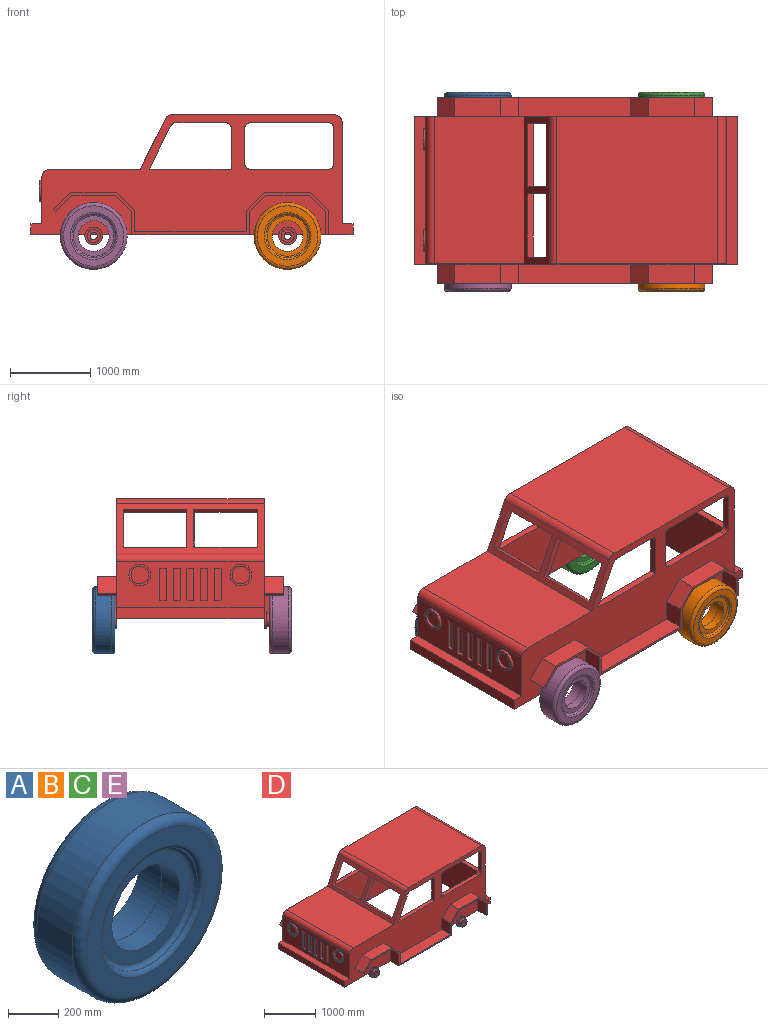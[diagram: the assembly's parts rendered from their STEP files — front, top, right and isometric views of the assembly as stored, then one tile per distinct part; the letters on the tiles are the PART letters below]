
ASSEMBLY  parts=5 mates=6
PART A: 11 faces, bbox 900.6x280x900.6 mm
  f0: torus R=292mm, axis (0,-1,0), area 55125.2mm2, adj f1,f10
  f1: plane 752x752mm, normal (0,-1,0), area 176281mm2, adj f0,f2
  f2: torus R=376mm, axis (0,-1,0), area 158491.9mm2, adj f1,f3
  f3: cylinder r=416mm len=832mm, axis (0,-1,0), area 522761mm2, adj f2,f4
  f4: torus R=376mm, axis (0,-1,0), area 158491.9mm2, adj f3,f5
  f5: plane 752x752mm, normal (0,1,0), area 308227.9mm2, adj f4,f6
  f6: cylinder r=208mm len=416mm, axis (0,-1,0), area 182966.4mm2, adj f5,f7
  f7: plane 416x416mm, normal (0,1,0), area 20106.2mm2, adj f6,f8
  f8: cylinder r=192mm len=384mm, axis (0,-1,0), area 120637.2mm2, adj f7,f9
  f9: plane 504x504mm, normal (0,-1,0), area 83692mm2, adj f8,f10
  f10: torus R=252mm, axis (0,-1,0), area 52256.1mm2, adj f0,f9
PART B: same geometry as A
PART C: same geometry as A
PART D: 174 faces, bbox 4012x2312x1623.2 mm
  f0: plane 1836x578mm, normal (-1,0,0), area 771594.2mm2, adj f3,f4,f19,f20,f74,f78,f149,f150
  f1: plane 81.89x27.55mm, normal (0,1,0), area 1632.8mm2, adj f11,f148
  f2: plane 81.89x27.55mm, normal (0,1,0), area 1632.8mm2, adj f11,f142
  f3: plane 4012x1496mm, normal (0,1,0), area 2936341.1mm2, adj f0,f11,f12,f13,f14,f15,f16,f17
  f4: plane 4012x1496mm, normal (0,-1,0), area 2936341.1mm2, adj f0,f11,f12,f13,f14,f15,f16,f17
  f5: plane 1666x1343mm, normal (-1,0,0), area 1386622mm2, adj f8,f9,f23,f24,f67,f68,f69,f70
  f6: plane 952.71x493.35mm, normal (0,-1,0), area 412746.6mm2, adj f11,f81,f82,f98,f99,f100,f132
  f7: plane 952.71x493.35mm, normal (0,1,0), area 412746.6mm2, adj f11,f102,f103,f119,f120,f121,f144
  f8: plane 3842x1411mm, normal (0,1,0), area 3073874.4mm2, adj f5,f10,f11,f13,f17,f23,f24,f25
  f9: plane 3842x1411mm, normal (0,-1,0), area 3073874.4mm2, adj f5,f10,f11,f13,f17,f23,f24,f25
  f10: plane 1666.02x670.62mm, normal (0.89,0,-0.45), area 415553.8mm2, adj f8,f9,f26,f27,f33,f34,f35,f36
  f11: plane 4012x2312mm, normal (0,0,-1), area 1666218.8mm2, adj f1,f2,f3,f4,f6,f7,f8,f9
  f12: plane 1836x136mm, normal (0,0,1), area 249696mm2, adj f3,f4,f13,f22
  f13: plane 1836x1258mm, normal (1,0,0), area 1458872mm2, adj f3,f4,f8,f9,f12,f14,f67,f68
  f14: cylinder r=102mm len=1836mm, axis (0,1,0), area 294166.2mm2, adj f3,f4,f13,f15
  f15: plane 2010.96x1836mm, normal (0,0,1), area 3692123.5mm2, adj f3,f4,f14,f16
  f16: cylinder r=102mm len=1836mm, axis (0,1,0), area 207338mm2, adj f3,f4,f15,f17
  f17: plane 1836.02x623.63mm, normal (-0.89,0,0.45), area 446562mm2, adj f3,f4,f8,f9,f16,f18,f33,f34
  f18: plane 1836x1122mm, normal (0,0,1), area 2059992mm2, adj f3,f4,f17,f19
  f19: cylinder r=102mm len=1836mm, axis (0,1,0), area 294166.2mm2, adj f0,f3,f4,f18
  f20: plane 1836x136mm, normal (0,0,1), area 249696mm2, adj f0,f3,f4,f21
  f21: plane 1836x136mm, normal (-1,0,0), area 249696mm2, adj f3,f4,f11,f20
  f22: plane 1836x136mm, normal (1,0,0), area 249696mm2, adj f3,f4,f11,f12
  f23: plane 1666x136mm, normal (0,0,-1), area 226576mm2, adj f5,f8,f9,f32
  f24: cylinder r=17mm len=1666mm, axis (0,1,0), area 44488.1mm2, adj f5,f8,f9,f25
  f25: plane 2010.96x1666mm, normal (0,0,-1), area 3350260.2mm2, adj f8,f9,f24,f26
  f26: cylinder r=17mm len=1666mm, axis (0,1,0), area 31356.7mm2, adj f8,f9,f10,f25
  f27: plane 1666x1174.53mm, normal (0,0,-1), area 1956771.8mm2, adj f8,f9,f10,f28
  f28: cylinder r=17mm len=1666mm, axis (0,1,0), area 44488.1mm2, adj f8,f9,f27,f29
  f29: plane 1666x663mm, normal (1,0,0), area 1104558mm2, adj f8,f9,f28,f30
  f30: plane 1666x136mm, normal (0,0,-1), area 226576mm2, adj f8,f9,f29,f31
  f31: plane 1666x51mm, normal (1,0,0), area 84966mm2, adj f8,f9,f11,f30
  f32: plane 1666x51mm, normal (-1,0,0), area 84966mm2, adj f8,f9,f11,f23
  f33: plane 790.52x76.05mm, normal (0.45,0,0.89), area 67192.5mm2, adj f8,f10,f17,f34
  f34: plane 509.58x311.81mm, normal (0,-1,0), area 44814mm2, adj f10,f17,f33,f35
  f35: plane 790.52x76.05mm, normal (-0.45,0,-0.89), area 67192.5mm2, adj f8,f10,f17,f34
  f36: plane 790.52x76.05mm, normal (-0.45,0,-0.89), area 67192.5mm2, adj f9,f10,f17,f37
  f37: plane 509.58x311.81mm, normal (0,1,0), area 44814mm2, adj f10,f17,f36,f38
  f38: plane 790.52x76.05mm, normal (0.45,0,0.89), area 67192.5mm2, adj f9,f10,f17,f37
  f39: plane 442x85mm, normal (1,0,0), area 37570mm2, adj f3,f9,f40,f46
  f40: cylinder r=68mm len=85mm, axis (0,-1,0), area 9079.2mm2, adj f3,f9,f39,f41
  f41: plane 973.96x85mm, normal (0,0,-1), area 82786.6mm2, adj f3,f9,f40,f42
  f42: cylinder r=68mm len=85mm, axis (0,-1,0), area 9079.2mm2, adj f3,f9,f41,f43
  f43: plane 442x85mm, normal (-1,0,0), area 37570mm2, adj f3,f9,f42,f44
  f44: cylinder r=68mm len=85mm, axis (0,-1,0), area 9079.2mm2, adj f3,f9,f43,f45
  f45: plane 973.96x85mm, normal (0,0,1), area 82786.6mm2, adj f3,f9,f44,f46
  f46: cylinder r=68mm len=85mm, axis (0,-1,0), area 9079.2mm2, adj f3,f9,f39,f45
  f47: plane 1020x85mm, normal (0,0,1), area 86700mm2, adj f3,f9,f48,f52
  f48: plane 540.41x270.21mm, normal (0.89,0,-0.45), area 51356.8mm2, adj f3,f9,f47,f49
  f49: cylinder r=68mm len=85mm, axis (0,-1,0), area 6399.3mm2, adj f3,f9,f48,f50
  f50: plane 620.97x85mm, normal (0,0,-1), area 52782.8mm2, adj f3,f9,f49,f51
  f51: cylinder r=68mm len=85mm, axis (0,-1,0), area 9079.2mm2, adj f3,f9,f50,f52
  f52: plane 510x85mm, normal (-1,0,0), area 43350mm2, adj f3,f9,f47,f51
  f53: cylinder r=68mm len=85mm, axis (0,-1,0), area 9079.2mm2, adj f4,f8,f54,f60
  f54: plane 973.96x85mm, normal (0,0,1), area 82786.6mm2, adj f4,f8,f53,f55
  f55: cylinder r=68mm len=85mm, axis (0,-1,0), area 9079.2mm2, adj f4,f8,f54,f56
  f56: plane 442x85mm, normal (-1,0,0), area 37570mm2, adj f4,f8,f55,f57
  f57: cylinder r=68mm len=85mm, axis (0,-1,0), area 9079.2mm2, adj f4,f8,f56,f58
  f58: plane 973.96x85mm, normal (0,0,-1), area 82786.6mm2, adj f4,f8,f57,f59
  f59: cylinder r=68mm len=85mm, axis (0,-1,0), area 9079.2mm2, adj f4,f8,f58,f60
  f60: plane 442x85mm, normal (1,0,0), area 37570mm2, adj f4,f8,f53,f59
  f61: plane 510x85mm, normal (-1,0,0), area 43350mm2, adj f4,f8,f62,f66
  f62: cylinder r=68mm len=85mm, axis (0,-1,0), area 9079.2mm2, adj f4,f8,f61,f63
  f63: plane 620.97x85mm, normal (0,0,-1), area 52782.8mm2, adj f4,f8,f62,f64
  f64: cylinder r=68mm len=85mm, axis (0,-1,0), area 6399.3mm2, adj f4,f8,f63,f65
  f65: plane 540.41x270.21mm, normal (0.89,0,-0.45), area 51356.8mm2, adj f4,f8,f64,f66
  f66: plane 1020x85mm, normal (0,0,1), area 86700mm2, adj f4,f8,f61,f65
  f67: plane 782x85mm, normal (0,0,-1), area 66470mm2, adj f5,f8,f13,f68
  f68: plane 544x85mm, normal (0,-1,0), area 46240mm2, adj f5,f13,f67,f69
  f69: plane 782x85mm, normal (0,0,1), area 66470mm2, adj f5,f8,f13,f68
  f70: plane 782x85mm, normal (0,0,-1), area 66470mm2, adj f5,f9,f13,f71
  f71: plane 544x85mm, normal (0,1,0), area 46240mm2, adj f5,f13,f70,f72
  f72: plane 782x85mm, normal (0,0,1), area 66470mm2, adj f5,f9,f13,f71
  f73: cylinder r=110.5mm len=221mm, axis (1,0,0), area 23605.9mm2, adj f75,f76
  f74: cylinder r=136mm len=272mm, axis (1,0,0), area 29053.4mm2, adj f0,f75
  f75: plane 272x272mm, normal (-1,0,0), area 19747.3mm2, adj f73,f74
  f76: plane 221x221mm, normal (-1,0,0), area 38359.6mm2, adj f73
  f77: cylinder r=110.5mm len=221mm, axis (1,0,0), area 23605.9mm2, adj f79,f80
  f78: cylinder r=136mm len=272mm, axis (1,0,0), area 29053.4mm2, adj f0,f79
  f79: plane 272x272mm, normal (-1,0,0), area 19747.3mm2, adj f77,f78
  f80: plane 221x221mm, normal (-1,0,0), area 38359.6mm2, adj f77
  f81: plane 238x204.35mm, normal (-0.71,0,-0.71), area 68782mm2, adj f6,f82,f100,f101
  f82: plane 289x238mm, normal (-1,0,0), area 68782mm2, adj f6,f11,f81,f101
  f83: plane 303.08x238mm, normal (1,0,0), area 72133.8mm2, adj f4,f11,f84,f101
  f84: plane 238x224.27mm, normal (0.71,0,0.71), area 75485.6mm2, adj f4,f83,f85,f101
  f85: plane 572.17x238mm, normal (0,0,1), area 136175.6mm2, adj f4,f84,f86,f101
  f86: plane 238x224.27mm, normal (-0.71,0,0.71), area 75485.6mm2, adj f4,f85,f87,f101
  f87: plane 269.08x238mm, normal (-1,0,0), area 64041.8mm2, adj f4,f86,f88,f101
  f88: plane 1394x238mm, normal (0,0,1), area 331772mm2, adj f4,f87,f89,f101
  f89: plane 269.08x238mm, normal (1,0,0), area 64041.8mm2, adj f4,f88,f90,f101
  f90: plane 238x224.27mm, normal (0.71,0,0.71), area 75485.6mm2, adj f4,f89,f91,f101
  f91: plane 572.17x238mm, normal (0,0,1), area 136175.6mm2, adj f4,f90,f92,f101
  f92: plane 238x214.31mm, normal (-0.71,0,0.71), area 72133.8mm2, adj f4,f91,f93,f101
  f93: plane 238x24.04mm, normal (-0.71,0,-0.71), area 8092mm2, adj f4,f92,f94,f101
  f94: plane 238x204.35mm, normal (0.71,0,-0.71), area 68782mm2, adj f4,f93,f95,f101
  f95: plane 544x238mm, normal (0,0,-1), area 129472mm2, adj f4,f94,f96,f101
  f96: plane 238x204.35mm, normal (-0.71,0,-0.71), area 68782mm2, adj f4,f95,f97,f101
  f97: plane 289x238mm, normal (-1,0,0), area 68782mm2, adj f4,f11,f96,f101
  f98: plane 289x238mm, normal (1,0,0), area 68782mm2, adj f6,f11,f99,f101
  f99: plane 238x204.35mm, normal (0.71,0,-0.71), area 68782mm2, adj f6,f98,f100,f101
  f100: plane 544x238mm, normal (0,0,-1), area 129472mm2, adj f6,f81,f99,f101
  f101: plane 3425.46x527.35mm, normal (0,-1,0), area 156521.8mm2, adj f11,f81,f82,f83,f84,f85,f86,f87
  f102: plane 238x204.35mm, normal (-0.71,0,-0.71), area 68782mm2, adj f7,f103,f121,f122
  f103: plane 289x238mm, normal (-1,0,0), area 68782mm2, adj f7,f11,f102,f122
  f104: plane 303.08x238mm, normal (1,0,0), area 72133.8mm2, adj f3,f11,f105,f122
  f105: plane 238x224.27mm, normal (0.71,0,0.71), area 75485.6mm2, adj f3,f104,f106,f122
  f106: plane 572.17x238mm, normal (0,0,1), area 136175.6mm2, adj f3,f105,f107,f122
  f107: plane 238x224.27mm, normal (-0.71,0,0.71), area 75485.6mm2, adj f3,f106,f108,f122
  f108: plane 269.08x238mm, normal (-1,0,0), area 64041.8mm2, adj f3,f107,f109,f122
  f109: plane 1394x238mm, normal (0,0,1), area 331772mm2, adj f3,f108,f110,f122
  f110: plane 269.08x238mm, normal (1,0,0), area 64041.8mm2, adj f3,f109,f111,f122
  f111: plane 238x224.27mm, normal (0.71,0,0.71), area 75485.6mm2, adj f3,f110,f112,f122
  f112: plane 572.17x238mm, normal (0,0,1), area 136175.6mm2, adj f3,f111,f113,f122
  f113: plane 238x214.31mm, normal (-0.71,0,0.71), area 72133.8mm2, adj f3,f112,f114,f122
  f114: plane 238x24.04mm, normal (-0.71,0,-0.71), area 8092mm2, adj f3,f113,f115,f122
  f115: plane 238x204.35mm, normal (0.71,0,-0.71), area 68782mm2, adj f3,f114,f116,f122
  f116: plane 544x238mm, normal (0,0,-1), area 129472mm2, adj f3,f115,f117,f122
  f117: plane 238x204.35mm, normal (-0.71,0,-0.71), area 68782mm2, adj f3,f116,f118,f122
  f118: plane 289x238mm, normal (-1,0,0), area 68782mm2, adj f3,f11,f117,f122
  f119: plane 289x238mm, normal (1,0,0), area 68782mm2, adj f7,f11,f120,f122
  f120: plane 238x204.35mm, normal (0.71,0,-0.71), area 68782mm2, adj f7,f119,f121,f122
  f121: plane 544x238mm, normal (0,0,-1), area 129472mm2, adj f7,f102,f120,f122
  f122: plane 3425.46x527.35mm, normal (0,1,0), area 156521.8mm2, adj f11,f102,f103,f104,f105,f106,f107,f108
  f123: cylinder r=44.2mm len=170mm, axis (0,-1,0), area 35448.4mm2, adj f11,f124,f129,f131
  f124: plane 81.89x27.55mm, normal (0,-1,0), area 1632.8mm2, adj f11,f123
  f125: cylinder r=44.2mm len=170mm, axis (0,-1,0), area 35448.4mm2, adj f11,f126,f134,f136
  f126: plane 81.89x27.55mm, normal (0,-1,0), area 1632.8mm2, adj f11,f125
  f127: cylinder r=110.5mm len=221mm, axis (0,1,0), area 23605.9mm2, adj f4,f128,f129
  f128: plane 221x221mm, normal (0,-1,0), area 17441.1mm2, adj f127,f130
  f129: plane 221x127.15mm, normal (0,1,0), area 18339.9mm2, adj f11,f123,f127
  f130: cylinder r=81.6mm len=163.2mm, axis (0,1,0), area 34864.1mm2, adj f128,f131
  f131: plane 163.2x163.2mm, normal (0,-1,0), area 14780.9mm2, adj f123,f130
  f132: cylinder r=110.5mm len=221mm, axis (0,1,0), area 23605.9mm2, adj f6,f133,f134
  f133: plane 221x221mm, normal (0,-1,0), area 17441.1mm2, adj f132,f135
  f134: plane 221x127.15mm, normal (0,1,0), area 18339.9mm2, adj f11,f125,f132
  f135: cylinder r=81.6mm len=163.2mm, axis (0,1,0), area 34864.1mm2, adj f133,f136
  f136: plane 163.2x163.2mm, normal (0,-1,0), area 14780.9mm2, adj f125,f135
  f137: plane 221x127.15mm, normal (0,-1,0), area 18339.9mm2, adj f11,f138,f142
  f138: cylinder r=110.5mm len=221mm, axis (0,-1,0), area 23605.9mm2, adj f3,f137,f139
  f139: plane 221x221mm, normal (0,1,0), area 17441.1mm2, adj f138,f140
  f140: cylinder r=81.6mm len=163.2mm, axis (0,-1,0), area 34864.1mm2, adj f139,f141
  f141: plane 163.2x163.2mm, normal (0,1,0), area 14780.9mm2, adj f140,f142
  f142: cylinder r=44.2mm len=102mm, axis (0,1,0), area 28327.1mm2, adj f2,f137,f141
  f143: plane 221x127.15mm, normal (0,-1,0), area 18339.9mm2, adj f11,f144,f148
  f144: cylinder r=110.5mm len=221mm, axis (0,-1,0), area 23605.9mm2, adj f7,f143,f145
  f145: plane 221x221mm, normal (0,1,0), area 17441.1mm2, adj f144,f146
  f146: cylinder r=81.6mm len=163.2mm, axis (0,-1,0), area 34864.1mm2, adj f145,f147
  f147: plane 163.2x163.2mm, normal (0,1,0), area 14780.9mm2, adj f146,f148
  f148: cylinder r=44.2mm len=102mm, axis (0,1,0), area 28327.1mm2, adj f1,f143,f147
  f149: plane 408x34mm, normal (0,-1,0), area 13872mm2, adj f0,f150,f152,f153
  f150: plane 85x34mm, normal (0,0,1), area 2890mm2, adj f0,f149,f151,f153
  f151: plane 408x34mm, normal (0,1,0), area 13872mm2, adj f0,f150,f152,f153
  f152: plane 85x34mm, normal (0,0,-1), area 2890mm2, adj f0,f149,f151,f153
  f153: plane 408x85mm, normal (-1,0,0), area 34680mm2, adj f149,f150,f151,f152
  f154: plane 408x34mm, normal (0,-1,0), area 13872mm2, adj f0,f155,f157,f158
  f155: plane 85x34mm, normal (0,0,1), area 2890mm2, adj f0,f154,f156,f158
  f156: plane 408x34mm, normal (0,1,0), area 13872mm2, adj f0,f155,f157,f158
  f157: plane 85x34mm, normal (0,0,-1), area 2890mm2, adj f0,f154,f156,f158
  f158: plane 408x85mm, normal (-1,0,0), area 34680mm2, adj f154,f155,f156,f157
  f159: plane 408x34mm, normal (0,-1,0), area 13872mm2, adj f0,f160,f162,f163
  f160: plane 85x34mm, normal (0,0,1), area 2890mm2, adj f0,f159,f161,f163
  f161: plane 408x34mm, normal (0,1,0), area 13872mm2, adj f0,f160,f162,f163
  f162: plane 85x34mm, normal (0,0,-1), area 2890mm2, adj f0,f159,f161,f163
  f163: plane 408x85mm, normal (-1,0,0), area 34680mm2, adj f159,f160,f161,f162
  f164: plane 408x34mm, normal (0,1,0), area 13872mm2, adj f0,f165,f167,f168
  f165: plane 85x34mm, normal (0,0,-1), area 2890mm2, adj f0,f164,f166,f168
  f166: plane 408x34mm, normal (0,-1,0), area 13872mm2, adj f0,f165,f167,f168
  f167: plane 85x34mm, normal (0,0,1), area 2890mm2, adj f0,f164,f166,f168
  f168: plane 408x85mm, normal (-1,0,0), area 34680mm2, adj f164,f165,f166,f167
  f169: plane 408x34mm, normal (0,-1,0), area 13872mm2, adj f0,f170,f172,f173
  f170: plane 85x34mm, normal (0,0,1), area 2890mm2, adj f0,f169,f171,f173
  f171: plane 408x34mm, normal (0,1,0), area 13872mm2, adj f0,f170,f172,f173
  f172: plane 85x34mm, normal (0,0,-1), area 2890mm2, adj f0,f169,f171,f173
  f173: plane 408x85mm, normal (-1,0,0), area 34680mm2, adj f169,f170,f171,f172
PART E: same geometry as A
PLACE A t=(-1637.42,1233.62,-603.2)mm
PLACE B t=(777.29,-965.11,-603.2)mm
PLACE C t=(777.29,1233.62,-603.2)mm
PLACE D t=(-447.07,14.2,-586.56)mm
PLACE E t=(-1637.42,-965.11,-603.2)mm
MATE cylindrical E.f0 <-> D.f123  axis (0,-1,0) through (-1637.42,-1035.11,-603.2)mm
MATE planar B.f0 <-> E.f0  axis (0,-1,0) through (777.29,-1245.11,-603.2)mm
MATE cylindrical C.f0 <-> D.f125  axis (0,1,0) through (777.29,1233.62,-603.2)mm
MATE planar C.f0 <-> A.f0  axis (0,1,0) through (777.29,1233.62,-603.2)mm
MATE cylindrical A.f0 <-> D.f123  axis (0,-1,0) through (-1637.42,1233.62,-603.2)mm
MATE cylindrical B.f0 <-> D.f125  axis (0,-1,0) through (777.29,-1105.11,-603.2)mm
